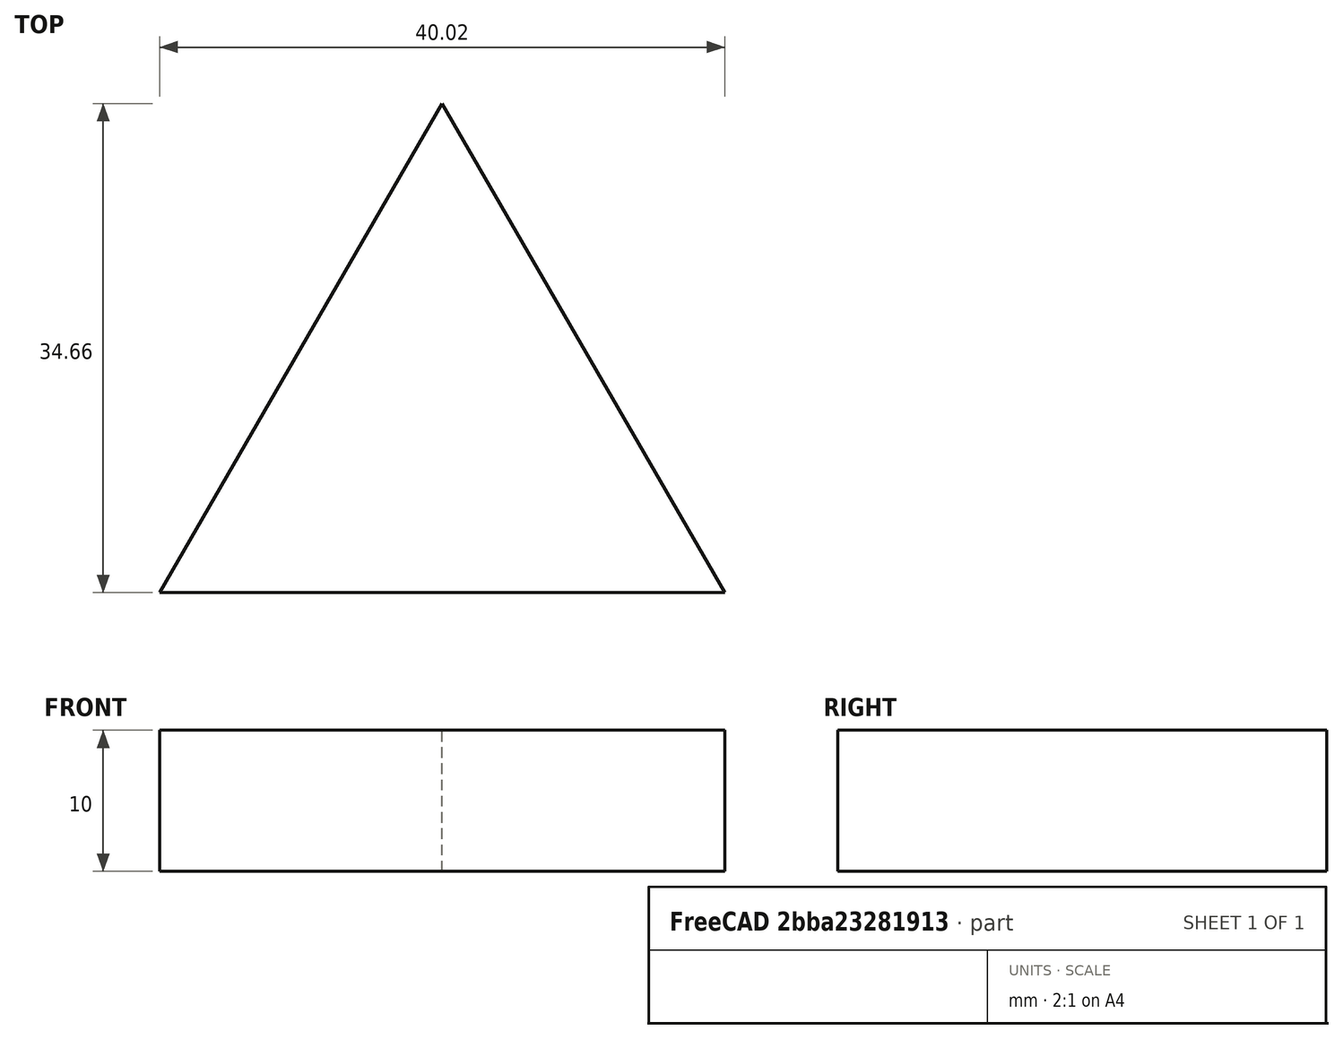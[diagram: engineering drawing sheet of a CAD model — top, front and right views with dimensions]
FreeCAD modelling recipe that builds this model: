
FCSTD DOCUMENT  (FreeCAD 0.21R33771 (Git))
Label: OJT1_T20P01_triangle
License: All rights reserved
LicenseURL: http://en.wikipedia.org/wiki/All_rights_reserved
objects: Sketcher::SketchObject×1, PartDesign::Pad×1, PartDesign::Body×1
note: 4 computed .brp shape members not serialized (recipe doc carries the construction recipe); baked Part::Feature solids carry a one-line shape summary decoded from their .brp

FEATURE [Sketcher::SketchObject] Sketch
  FullyConstrained = true
  MapMode = 5
  Support = -> [XY_Plane]
  sketch-geometry (4):
    g0: LineSegment StartX=-20.011 StartY=-17.33 StartZ=0 EndX=0 EndY=17.33 EndZ=0
    g1: LineSegment StartX=0 StartY=17.33 StartZ=0 EndX=20.011 EndY=-17.33 EndZ=0
    g2: LineSegment StartX=20.011 StartY=-17.33 StartZ=0 EndX=-20.011 EndY=-17.33 EndZ=0
    g3: LineSegment StartX=0 StartY=17.33 StartZ=0 EndX=0 EndY=-17.33 EndZ=0
  constraints (10):
    c: Coincident(g0,g1)
    c: Coincident(g1,g2)
    c: Coincident(g2,g0)
    c: PointOnObject(g3,g2)
    c: Coincident(g3,g0)
    c: Symmetric(g0,g1,g3)
    c: Symmetric(g0,g3,g-1)
    c: PointOnObject(g0,g-2)
    c: Angle(g2,g0) = 1.0472
    c: DistanceY(g3,g3) = 34.66
FEATURE [PartDesign::Pad] Pad
  Direction = (0,0,1)
  Length = 10
  Length2 = 10
  Profile = -> Sketch
  ReferenceAxis = -> Sketch [N_Axis]
  Type = 0
FEATURE [PartDesign::Body] Body
  Group = -> [Sketch,Pad]
  Origin = -> Origin
  Tip = -> Pad
